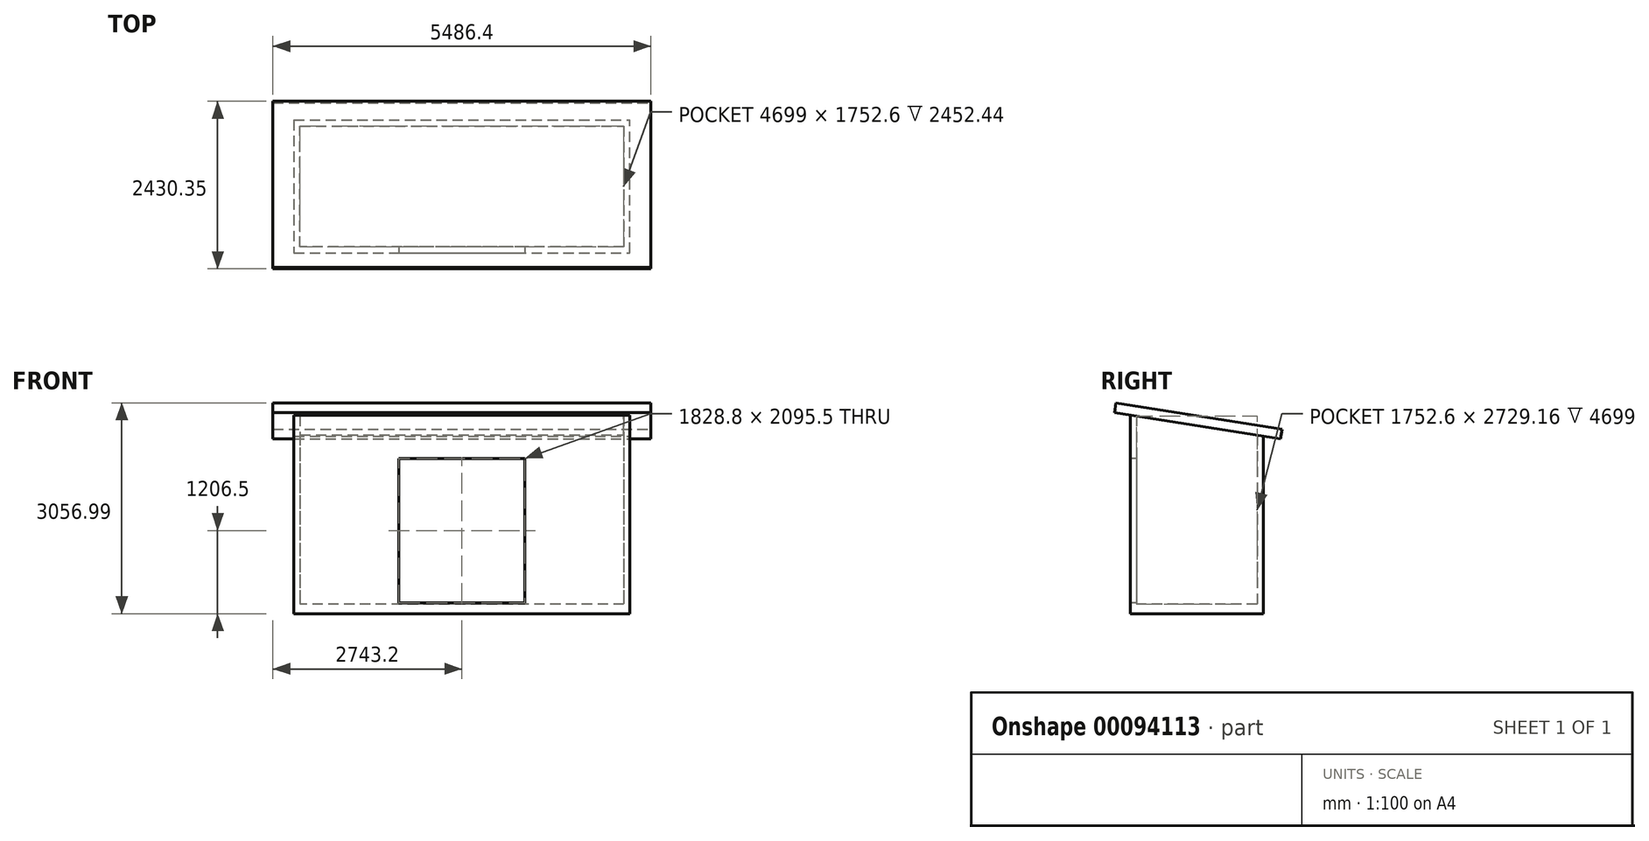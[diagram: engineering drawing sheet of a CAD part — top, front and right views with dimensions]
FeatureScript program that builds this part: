
annotation { "Feature Type Name" : "Feature", "Feature Type Description" : "" }
export const myFeature = defineFeature(function(context is Context, id is Id, definition is map)
    precondition{}
    {
        {
            var Q0;
            Q0=qCreatedBy(makeId("Top.planeOp"),FACE);
            var sketch = newSketch(context, id + "F0", { "sketchPlane" : qUnion([Q0])});
            skLineSegment(sketch, "E0.bottom", {"start": v(0, 0) * mm, "end": v(4876.8, 0) * mm});
            skLineSegment(sketch, "E0.top", {"start": v(0, 1930.4) * mm, "end": v(4876.8, 1930.4) * mm});
            skLineSegment(sketch, "E0.left", {"start": v(0, 0) * mm, "end": v(0, 1930.4) * mm});
            skLineSegment(sketch, "E0.right", {"start": v(4876.8, 0) * mm, "end": v(4876.8, 1930.4) * mm});
            skSolve(sketch);
        }
        {
            var Q0;
            Q0=makeQuery(id+"F0.imprint","IMPRINT",FACE,{"disambiguationData":[TD([[makeQuery(id+"F0.imprint","IMPRINT",EDGE,{"derivedFrom":sQuery(id+"F0.wireOp",EDGE,"E0.bottom")}),1.0]])]});
            extrude(context, id + "F1", {"entities" : qUnion([Q0]), "depth" : 139.7 * mm});
        }
        {
            var Q0;
            Q0=makeQuery(id+"F1.opExtrude","CAP_FACE",FACE,{"disambiguationData":[OSD([sQuery(id+"F0.wireOp",EDGE,"E0.bottom"),sQuery(id+"F0.wireOp",EDGE,"E0.top"),sQuery(id+"F0.wireOp",EDGE,"E0.left"),sQuery(id+"F0.wireOp",EDGE,"E0.right")])],"isStart":false});
            var sketch = newSketch(context, id + "F2", { "sketchPlane" : qUnion([Q0])});
            skLineSegment(sketch, "E1.0", {"start": v(88.9, 1841.5) * mm, "end": v(88.9, 88.9) * mm});
            skLineSegment(sketch, "E1.1", {"start": v(4787.9, 1841.5) * mm, "end": v(88.9, 1841.5) * mm});
            skLineSegment(sketch, "E1.2", {"start": v(4787.9, 88.9) * mm, "end": v(4787.9, 1841.5) * mm});
            skLineSegment(sketch, "E1.3", {"start": v(88.9, 88.9) * mm, "end": v(4787.9, 88.9) * mm});
            skLineSegment(sketch, "E2.0", {"start": v(0, 0) * mm, "end": v(0, 1930.4) * mm});
            skLineSegment(sketch, "E3.0", {"start": v(0, 1930.4) * mm, "end": v(4876.8, 1930.4) * mm});
            skLineSegment(sketch, "E4.0", {"start": v(4876.8, 0) * mm, "end": v(4876.8, 1930.4) * mm});
            skLineSegment(sketch, "E5.0", {"start": v(0, 0) * mm, "end": v(4876.8, 0) * mm});
            skSolve(sketch);
        }
        {
            var Q0;
            Q0=makeQuery(id+"F2.imprint","IMPRINT",FACE,{"disambiguationData":[TD([[makeQuery(id+"F2.imprint","IMPRINT",EDGE,{"derivedFrom":sQuery(id+"F2.wireOp",EDGE,"E1.0")}),-1.0]])]});
            extrude(context, id + "F3", {"entities" : qUnion([Q0]), "operationType" : NewBodyOperationType.ADD, "depth" : 2743.2 * mm});
        }
        {
            var Q0;
            Q0=makeQuery(id+"F3.boolean.opBoolean","MERGE",FACE,{"derivedFrom":[makeQuery(id+"F1.opExtrude","SWEPT_FACE",FACE,{"disambiguationData":[OSD([sQuery(id+"F0.wireOp",EDGE,"E0.right")])]}),makeQuery(id+"F3.opExtrude","SWEPT_FACE",FACE,{"disambiguationData":[OSD([sQuery(id+"F2.wireOp",EDGE,"E4.0")])]})]});
            var sketch = newSketch(context, id + "F4", { "sketchPlane" : qUnion([Q0])});
            skLineSegment(sketch, "E6.0", {"start": v(1930.4, 2882.9) * mm, "end": v(1930.4, 0) * mm});
            skLineSegment(sketch, "E7.0", {"start": v(0, 2882.9) * mm, "end": v(1930.4, 2882.9) * mm});
            skLineSegment(sketch, "E8", {"start": v(0, 2882.9) * mm, "end": v(1930.4, 2578.1) * mm});
            skSolve(sketch);
        }
        {
            var Q0;
            {var subQ0=sQuery(id+"F4.wireOp",EDGE,"E7.0");Q0=makeQuery(id+"F4.imprint","IMPRINT",FACE,{"disambiguationData":[TD([[makeQuery(id+"F4.imprint","IMPRINT",EDGE,{"derivedFrom":subQ0}),-1.0]])]});}
            extrude(context, id + "F5", {"entities" : qUnion([Q0]), "operationType" : NewBodyOperationType.REMOVE, "endBound" : BoundingType.THROUGH_ALL, "oppositeDirection" : true, "depth" : 25.4 * mm});
        }
        {
            var Q0;
            Q0=makeQuery(id+"F3.boolean.opBoolean","MERGE",FACE,{"derivedFrom":[makeQuery(id+"F1.opExtrude","SWEPT_FACE",FACE,{"disambiguationData":[OSD([sQuery(id+"F0.wireOp",EDGE,"E0.right")])]}),makeQuery(id+"F3.opExtrude","SWEPT_FACE",FACE,{"disambiguationData":[OSD([sQuery(id+"F2.wireOp",EDGE,"E4.0")])]})]});
            var sketch = newSketch(context, id + "F6", { "sketchPlane" : qUnion([Q0])});
            skLineSegment(sketch, "E9.0", {"start": v(0, 2882.9) * mm, "end": v(1930.4, 2578.1) * mm});
            skLineSegment(sketch, "E10", {"start": v(-228.6, 2919) * mm, "end": v(2179.96, 2538.7) * mm});
            skLineSegment(sketch, "E11", {"start": v(2179.96, 2538.7) * mm, "end": v(2201.75, 2676.69) * mm});
            skLineSegment(sketch, "E12", {"start": v(2201.75, 2676.69) * mm, "end": v(-206.81, 3056.99) * mm});
            skLineSegment(sketch, "E13", {"start": v(-206.81, 3056.99) * mm, "end": v(-228.6, 2919) * mm});
            skSolve(sketch);
        }
        {
            var Q0;
            {var subQ0=sQuery(id+"F6.wireOp",EDGE,"E11");Q0=makeQuery(id+"F6.imprint","IMPRINT",FACE,{"disambiguationData":[TD([[makeQuery(id+"F6.imprint","IMPRINT",EDGE,{"derivedFrom":subQ0}),1.0]])]});}
            extrude(context, id + "F7", {"entities" : qUnion([Q0]), "operationType" : NewBodyOperationType.ADD, "oppositeDirection" : true, "depth" : 5181.6 * mm, "hasSecondDirection" : true, "secondDirectionOppositeDirection" : false, "secondDirectionDepth" : 304.8 * mm});
        }
        {
            var Q0;
            Q0=makeQuery(id+"F3.boolean.opBoolean","MERGE",FACE,{"derivedFrom":[makeQuery(id+"F1.opExtrude","SWEPT_FACE",FACE,{"disambiguationData":[OSD([sQuery(id+"F0.wireOp",EDGE,"E0.bottom")])]}),makeQuery(id+"F3.opExtrude","SWEPT_FACE",FACE,{"disambiguationData":[OSD([sQuery(id+"F2.wireOp",EDGE,"E5.0")])]})]});
            var sketch = newSketch(context, id + "F8", { "sketchPlane" : qUnion([Q0])});
            skLineSegment(sketch, "E14.bottom", {"start": v(1524, 0) * mm, "end": v(3352.8, 0) * mm});
            skLineSegment(sketch, "E14.top", {"start": v(1524, 2254.25) * mm, "end": v(3352.8, 2254.25) * mm});
            skLineSegment(sketch, "E14.left", {"start": v(3352.8, 0) * mm, "end": v(3352.8, 2254.25) * mm});
            skLineSegment(sketch, "E14.right", {"start": v(1524, 0) * mm, "end": v(1524, 2254.25) * mm});
            skPoint(sketch, "E15", {"position": v(2438.4, 0) * mm});
            skLineSegment(sketch, "E16", {"start": v(1524, 158.75) * mm, "end": v(3352.8, 158.75) * mm});
            skSolve(sketch);
        }
        {
            var Q0;
            {var subQ0=sQuery(id+"F8.wireOp",EDGE,"E14.top");Q0=makeQuery(id+"F8.imprint","IMPRINT",FACE,{"disambiguationData":[TD([[makeQuery(id+"F8.imprint","IMPRINT",EDGE,{"derivedFrom":subQ0}),-1.0]])]});}
            extrude(context, id + "F9", {"entities" : qUnion([Q0]), "operationType" : NewBodyOperationType.REMOVE, "oppositeDirection" : true, "depth" : 304.8 * mm});
        }
    });
